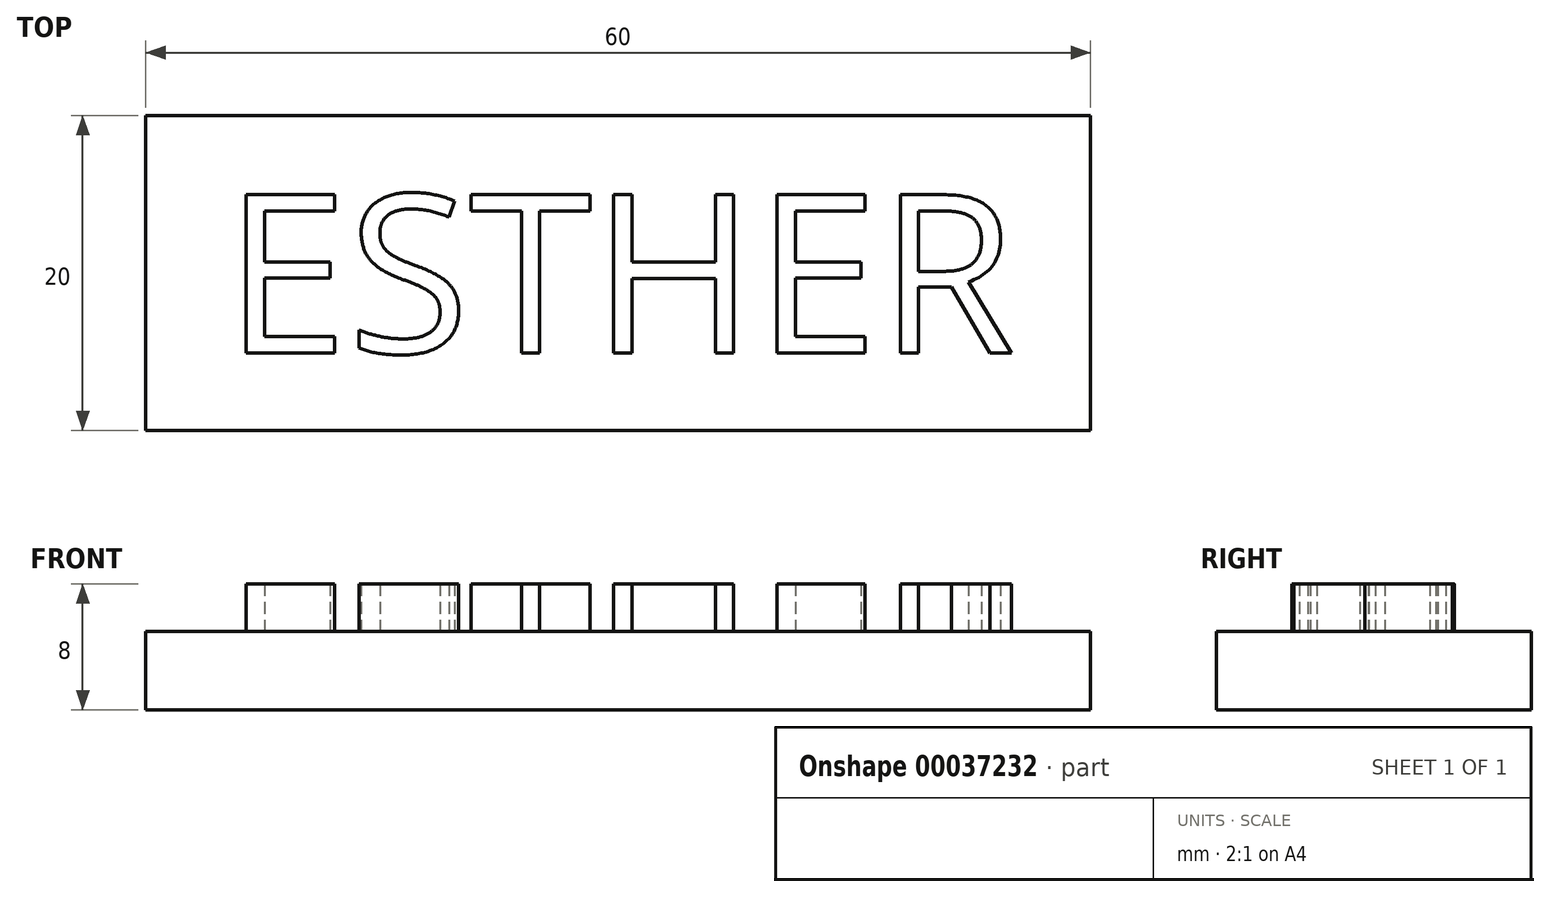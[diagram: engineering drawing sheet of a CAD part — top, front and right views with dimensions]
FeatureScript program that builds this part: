
annotation { "Feature Type Name" : "Feature", "Feature Type Description" : "" }
export const myFeature = defineFeature(function(context is Context, id is Id, definition is map)
    precondition{}
    {
        {
            var Q0;
            Q0=qCreatedBy(makeId("Top.planeOp"),FACE);
            var sketch = newSketch(context, id + "F0", { "sketchPlane" : qUnion([Q0])});
            skLineSegment(sketch, "E0.rect.bottom", {"start": v(-30, 10) * mm, "end": v(30, 10) * mm});
            skLineSegment(sketch, "E0.rect.top", {"start": v(-30, -10) * mm, "end": v(30, -10) * mm});
            skLineSegment(sketch, "E0.rect.left", {"start": v(-30, 10) * mm, "end": v(-30, -10) * mm});
            skLineSegment(sketch, "E0.rect.right", {"start": v(30, 10) * mm, "end": v(30, -10) * mm});
            skPoint(sketch, "E0.rect.middle", {"position": v(0, 0) * mm});
            skSolve(sketch);
        }
        {
            var Q0;
            Q0 = qSketchRegion(id + "F0", true);
            extrude(context, id + "F1", {"entities" : qUnion([Q0]), "depth" : 5 * mm});
        }
        {
            var Q0;
            Q0=makeQuery(id+"F1.opExtrude","CAP_FACE",FACE,{"disambiguationData":[OSD([sQuery(id+"F0.wireOp",EDGE,"E0.rect.bottom"),sQuery(id+"F0.wireOp",EDGE,"E0.rect.top"),sQuery(id+"F0.wireOp",EDGE,"E0.rect.left"),sQuery(id+"F0.wireOp",EDGE,"E0.rect.right")])],"isStart":false});
            var sketch = newSketch(context, id + "F2", { "sketchPlane" : qUnion([Q0])});
            skText(sketch, "E1", { "text": "ESTHER", "fontName": "OpenSans-Regular.ttf"});
            const initialGuessF2  = {"E1": [-0.025, -0.00507, 1, 0, 0.01013]};
            skSetInitialGuess(sketch, initialGuessF2);
            skSolve(sketch);
        }
        {
            var Q0;
            Q0 = qSketchRegion(id + "F2", true);
            extrude(context, id + "F3", {"entities" : qUnion([Q0]), "operationType" : NewBodyOperationType.ADD, "depth" : 3 * mm});
        }
    });
